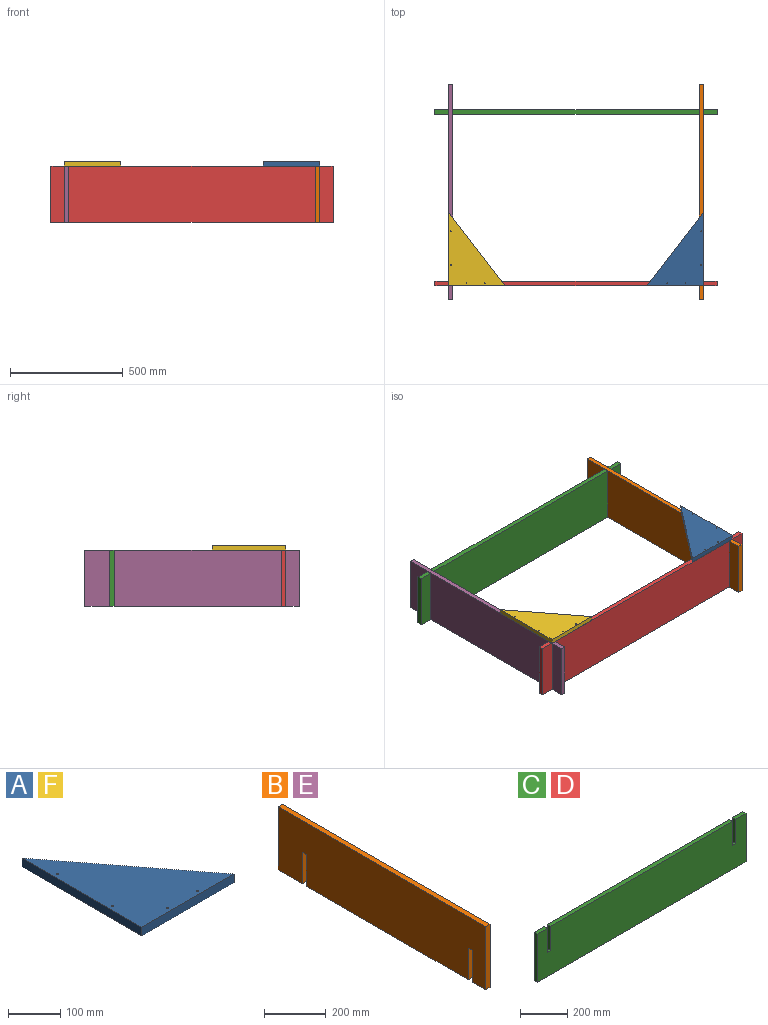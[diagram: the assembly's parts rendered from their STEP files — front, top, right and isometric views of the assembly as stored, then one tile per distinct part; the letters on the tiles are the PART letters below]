
ASSEMBLY  parts=6 mates=5
PART A: 9 faces, bbox 250x325x20 mm
  f0: plane 250x20mm, normal (0,-1,0), area 5000mm2, adj f1,f2,f3,f4
  f1: plane 325x250mm, normal (0.79,0.61,0), area 8200.6mm2, adj f0,f2,f3,f4
  f2: plane 325x20mm, normal (-1,0,0), area 6500mm2, adj f0,f1,f3,f4
  f3: plane 325x250mm, normal (0,0,1), area 40574.7mm2, adj f0,f1,f2,f5,f6,f7,f8
  f4: plane 325x250mm, normal (0,0,-1), area 40574.7mm2, adj f0,f1,f2,f5,f6,f7,f8
  f5: cylinder r=2mm len=20mm, axis (0,0,-1), area 251.3mm2, adj f3,f4
  f6: cylinder r=2mm len=20mm, axis (0,0,-1), area 251.3mm2, adj f3,f4
  f7: cylinder r=2mm len=20mm, axis (0,0,-1), area 251.3mm2, adj f3,f4
  f8: cylinder r=2mm len=20mm, axis (0,0,-1), area 251.3mm2, adj f3,f4
PART B: 14 faces, bbox 20x950x250 mm
  f0: plane 110x20mm, normal (0,0,-1), area 2200mm2, adj f1,f11,f12,f13
  f1: plane 250x20mm, normal (0,1,0), area 5000mm2, adj f0,f2,f12,f13
  f2: plane 950x20mm, normal (0,0,1), area 19000mm2, adj f1,f3,f12,f13
  f3: plane 250x20mm, normal (0,-1,0), area 5000mm2, adj f2,f4,f12,f13
  f4: plane 60x20mm, normal (0,0,-1), area 1200mm2, adj f3,f5,f12,f13
  f5: plane 125x20mm, normal (0,1,0), area 2500mm2, adj f4,f6,f12,f13
  f6: plane 20x20mm, normal (0,0,-1), area 400mm2, adj f5,f7,f12,f13
  f7: plane 125x20mm, normal (0,-1,0), area 2500mm2, adj f6,f8,f12,f13
  f8: plane 740x20mm, normal (0,0,-1), area 14800mm2, adj f7,f9,f12,f13
  f9: plane 125x20mm, normal (0,1,0), area 2500mm2, adj f8,f10,f12,f13
  f10: plane 20x20mm, normal (0,0,-1), area 400mm2, adj f9,f11,f12,f13
  f11: plane 125x20mm, normal (0,-1,0), area 2500mm2, adj f0,f10,f12,f13
  f12: plane 950x250mm, normal (1,0,0), area 232500mm2, adj f0,f1,f2,f3,f4,f5,f6,f7
  f13: plane 950x250mm, normal (-1,0,0), area 232500mm2, adj f0,f1,f2,f3,f4,f5,f6,f7
PART C: 14 faces, bbox 1250x20x250 mm
  f0: plane 125x20mm, normal (-1,0,0), area 2500mm2, adj f1,f11,f12,f13
  f1: plane 20x20mm, normal (0,0,1), area 400mm2, adj f0,f2,f12,f13
  f2: plane 125x20mm, normal (1,0,0), area 2500mm2, adj f1,f3,f12,f13
  f3: plane 1090x20mm, normal (0,0,1), area 21800mm2, adj f2,f4,f12,f13
  f4: plane 125x20mm, normal (-1,0,0), area 2500mm2, adj f3,f5,f12,f13
  f5: plane 20x20mm, normal (0,0,1), area 400mm2, adj f4,f6,f12,f13
  f6: plane 125x20mm, normal (1,0,0), area 2500mm2, adj f5,f7,f12,f13
  f7: plane 60x20mm, normal (0,0,1), area 1200mm2, adj f6,f8,f12,f13
  f8: plane 250x20mm, normal (-1,0,0), area 5000mm2, adj f7,f9,f12,f13
  f9: plane 1250x20mm, normal (0,0,-1), area 25000mm2, adj f8,f10,f12,f13
  f10: plane 250x20mm, normal (1,0,0), area 5000mm2, adj f9,f11,f12,f13
  f11: plane 60x20mm, normal (0,0,1), area 1200mm2, adj f0,f10,f12,f13
  f12: plane 1250x250mm, normal (0,-1,0), area 307500mm2, adj f0,f1,f2,f3,f4,f5,f6,f7
  f13: plane 1250x250mm, normal (0,1,0), area 307500mm2, adj f0,f1,f2,f3,f4,f5,f6,f7
PART D: same geometry as C
PART E: same geometry as B
PART F: same geometry as A
PLACE A rot(axis=(0,1,0),180deg) t=(440,142.5,145)mm
PLACE B t=(545,395,0)mm
PLACE C t=(0,760,0)mm
PLACE D at identity fixed
PLACE E t=(-565,395,0)mm
PLACE F t=(-440,142.5,125)mm
MATE fastened B.f10 <-> C.f1  axis (0,0,-1) through (555,750,0)mm
MATE fastened E.f6 <-> D.f5  axis (0,0,-1) through (-555,-10,0)mm
MATE fastened D.f1 <-> B.f6  axis (0,0,1) through (555,-10,0)mm
MATE fastened F.f4 <-> D.f3  axis (0,0,-1) through (0,-10,125)mm
MATE fastened A.f8 <-> F.f4  axis (0,0,-1) through (405,-10,125)mm
